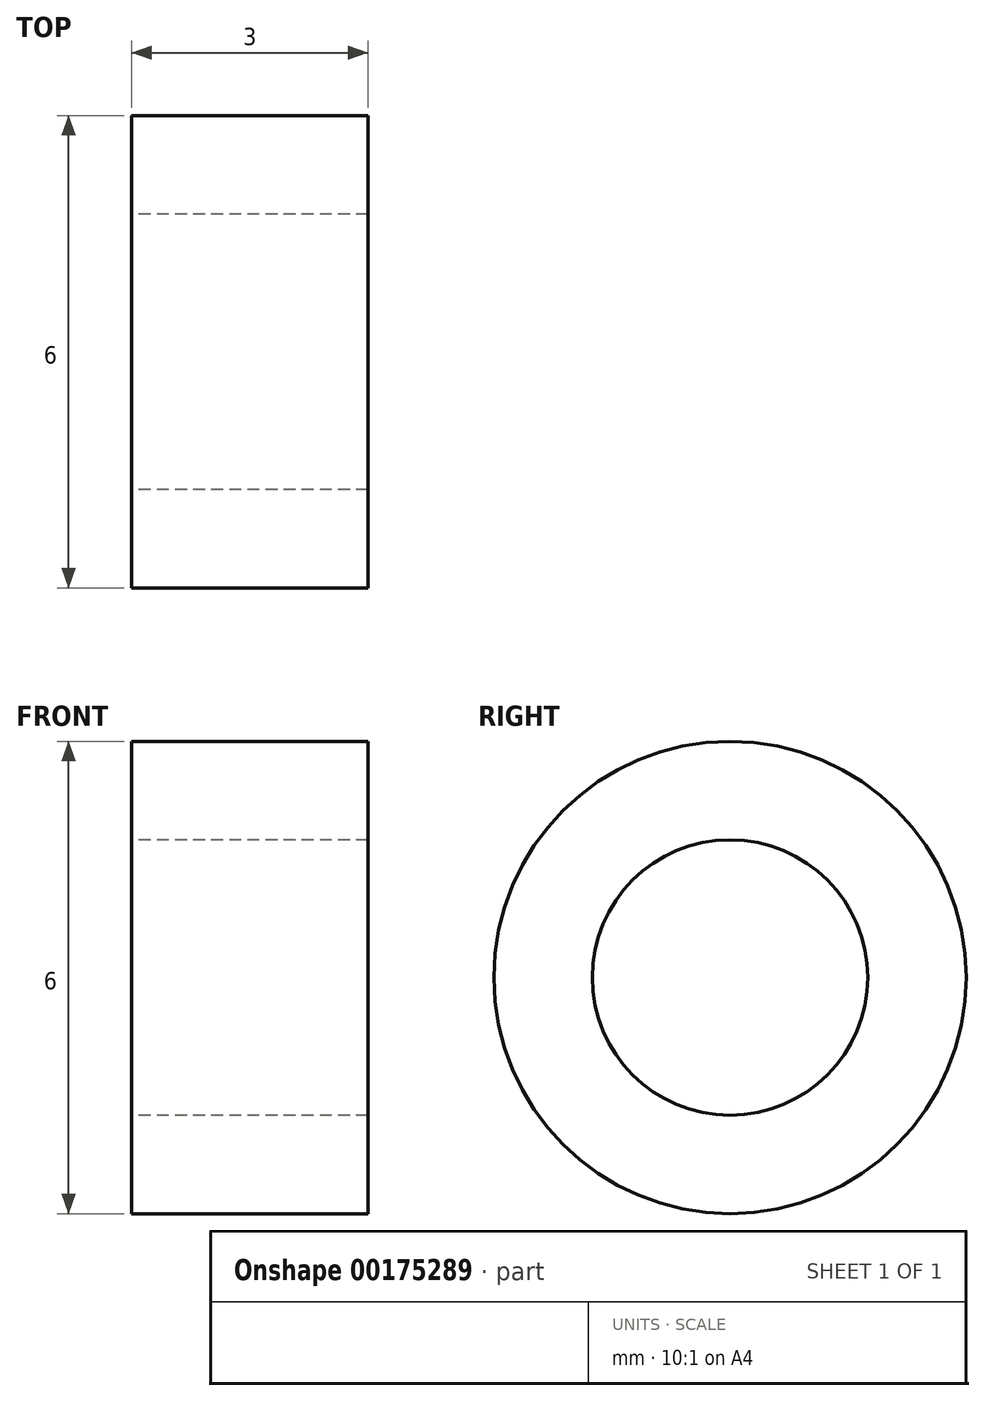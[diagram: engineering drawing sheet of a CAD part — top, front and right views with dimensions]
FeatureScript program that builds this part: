
annotation { "Feature Type Name" : "Feature", "Feature Type Description" : "" }
export const myFeature = defineFeature(function(context is Context, id is Id, definition is map)
    precondition{}
    {
        {
            var Q0;
            Q0=qCreatedBy(makeId("Right.planeOp"),FACE);
            var sketch = newSketch(context, id + "F0", { "sketchPlane" : qUnion([Q0])});
            skCircle(sketch, "E0", {"center": v(0, 0) * mm, "radius": 3 * mm});
            skCircle(sketch, "E1", {"center": v(0, 0) * mm, "radius": 1.75 * mm});
            skSolve(sketch);
        }
        {
            var Q0;
            Q0=qSketchRegion(id+"F0",true);
            extrude(context, id + "F1", {"entities" : qUnion([Q0]), "depth" : 3 * mm});
        }
    });
